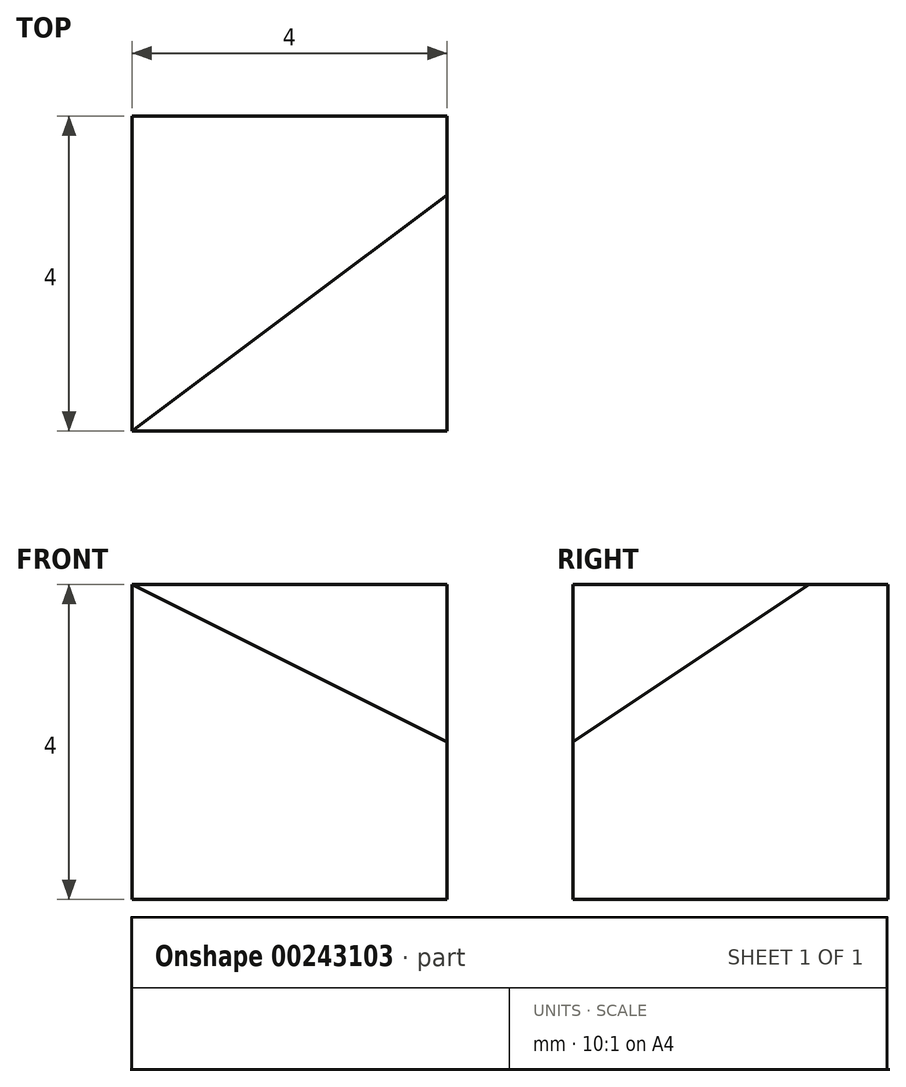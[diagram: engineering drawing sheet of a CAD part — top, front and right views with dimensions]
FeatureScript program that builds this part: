
annotation { "Feature Type Name" : "Feature", "Feature Type Description" : "" }
export const myFeature = defineFeature(function(context is Context, id is Id, definition is map)
    precondition{}
    {
        {
            var Q0;
            Q0=qCreatedBy(makeId("Top.planeOp"),FACE);
            var sketch = newSketch(context, id + "F0", { "sketchPlane" : qUnion([Q0])});
            skLineSegment(sketch, "E0.bottom", {"start": v(0, 0) * mm, "end": v(4, 0) * mm});
            skLineSegment(sketch, "E0.top", {"start": v(0, 4) * mm, "end": v(4, 4) * mm});
            skLineSegment(sketch, "E0.left", {"start": v(0, 0) * mm, "end": v(0, 4) * mm});
            skLineSegment(sketch, "E0.right", {"start": v(4, 0) * mm, "end": v(4, 4) * mm});
            skSolve(sketch);
        }
        {
            var Q0;
            Q0=makeQuery(id+"F0.imprint","IMPRINT",FACE,{"disambiguationData":[TD([[makeQuery(id+"F0.imprint","IMPRINT",EDGE,{"derivedFrom":sQuery(id+"F0.wireOp",EDGE,"E0.bottom")}),1.0]])]});
            extrude(context, id + "F1", {"entities" : qUnion([Q0]), "depth" : 4 * mm});
        }
        {
            var Q0;
            Q0=makeQuery(id+"F1.opExtrude","SWEPT_FACE",FACE,{"disambiguationData":[OSD([sQuery(id+"F0.wireOp",EDGE,"E0.right")])]});
            var sketch = newSketch(context, id + "F2", { "sketchPlane" : qUnion([Q0])});
            skLineSegment(sketch, "E1", {"start": v(0, 0) * mm, "end": v(0, 2) * mm, "construction": true});
            skLineSegment(sketch, "E2", {"start": v(4, 4) * mm, "end": v(3, 4) * mm});
            skLineSegment(sketch, "E3", {"start": v(3, 4) * mm, "end": v(0, 2) * mm, "construction": true});
            skSolve(sketch);
        }
        {
            var Q0;
            Q0=makeQuery(id+"F1.opExtrude","SWEPT_FACE",FACE,{"disambiguationData":[OSD([sQuery(id+"F0.wireOp",EDGE,"E0.bottom")])]});
            var sketch = newSketch(context, id + "F3", { "sketchPlane" : qUnion([Q0])});
            skLineSegment(sketch, "E4", {"start": v(0, 4) * mm, "end": v(4, 2) * mm, "construction": true});
            skSolve(sketch);
        }
        {
            var Q0;
            Q0=sQuery(id+"F2.wireOp",VERTEX,"E3.start");
            var Q1;
            Q1=sQuery(id+"F3.wireOp",VERTEX,"E4.end");
            var Q2;
            Q2=sQuery(id+"F3.wireOp",VERTEX,"E4.start");
            cPlane(context, id + "F4", {"entities" : qUnion([Q0, Q1, Q2]), "cplaneType" : CPlaneType.THREE_POINT, "offset" : 25 * mm, "width" : 150 * mm, "height" : 150 * mm});
        }
        {
            var Q0;
            Q0=qCreatedBy(id+"F4.planeOp",FACE);
            var sketch = newSketch(context, id + "F5", { "sketchPlane" : qUnion([Q0])});
            skPoint(sketch, "E5.0", {"position": v(-1.28, 2.22) * mm});
            skPoint(sketch, "E5.1", {"position": v(3.05, 4.71) * mm});
            skPoint(sketch, "E5.2", {"position": v(3.05, 1.1) * mm});
            skLineSegment(sketch, "E6", {"start": v(-1.28, 2.22) * mm, "end": v(3.05, 4.71) * mm, "construction": true});
            skLineSegment(sketch, "E7", {"start": v(3.05, 1.1) * mm, "end": v(-1.28, 2.22) * mm, "construction": true});
            skLineSegment(sketch, "E8", {"start": v(3.05, 1.1) * mm, "end": v(3.05, 4.71) * mm, "construction": true});
            skLineSegment(sketch, "E9", {"start": v(-1.28, 2.22) * mm, "end": v(3.05, 4.71) * mm});
            skLineSegment(sketch, "E10", {"start": v(3.05, 1.1) * mm, "end": v(3.05, 4.71) * mm});
            skLineSegment(sketch, "E11", {"start": v(3.05, 1.1) * mm, "end": v(-1.28, 2.22) * mm});
            skSolve(sketch);
        }
        {
            var Q0;
            Q0 = qSketchRegion(id + "F5", true);
            extrude(context, id + "F6", {"entities" : qUnion([Q0]), "operationType" : NewBodyOperationType.REMOVE, "endBound" : BoundingType.THROUGH_ALL, "depth" : 25 * mm});
        }
    });
